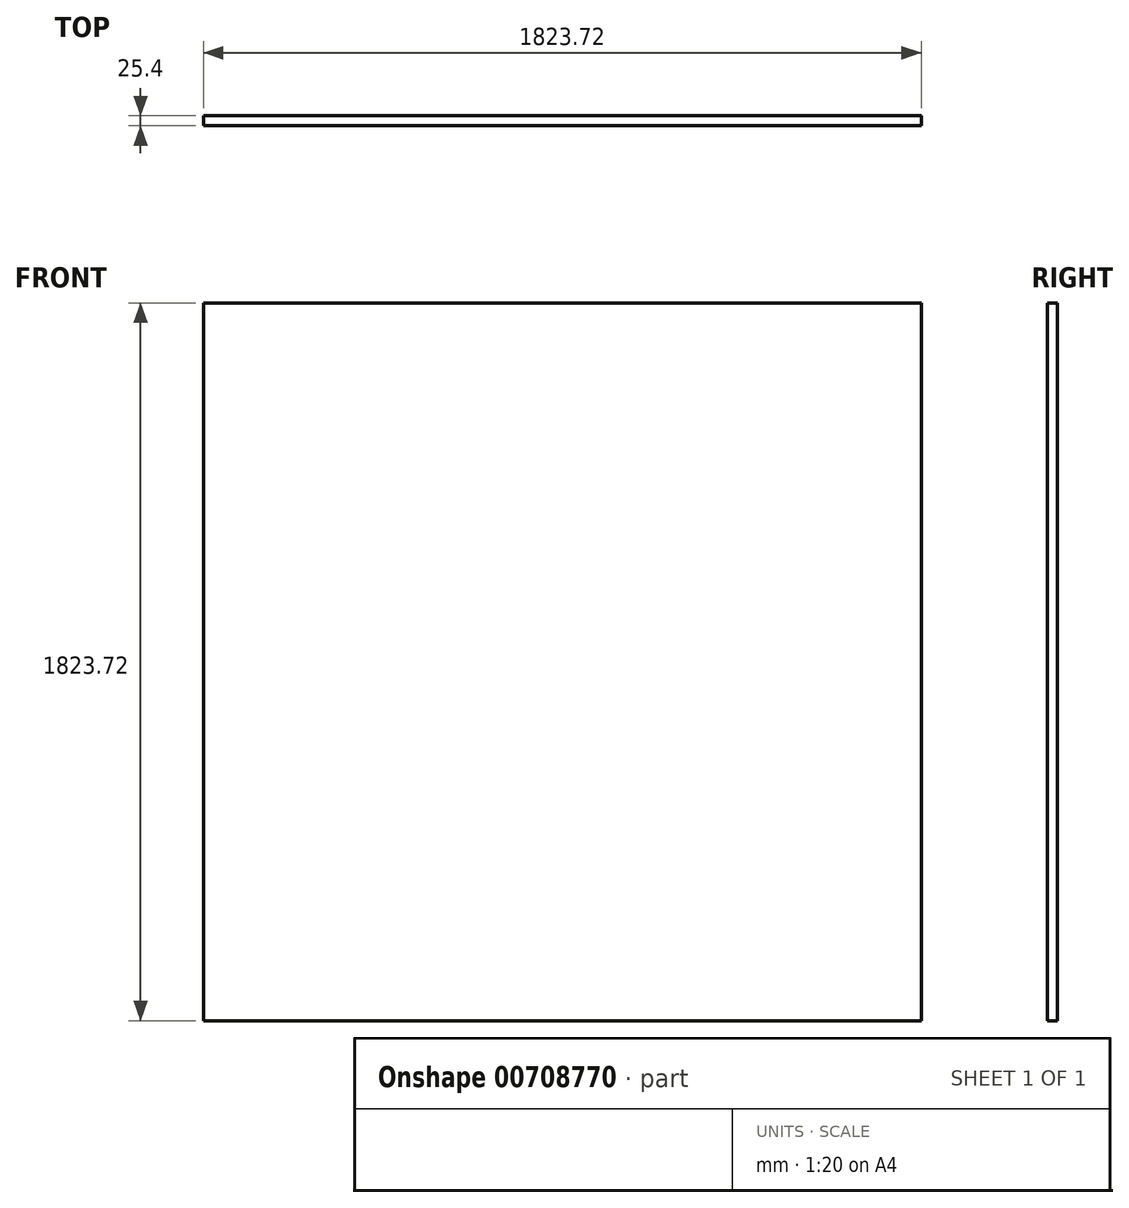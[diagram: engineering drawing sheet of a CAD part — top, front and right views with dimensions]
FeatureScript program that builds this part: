
annotation { "Feature Type Name" : "Feature", "Feature Type Description" : "" }
export const myFeature = defineFeature(function(context is Context, id is Id, definition is map)
    precondition{}
    {
        {
            var Q0;
            Q0=qCreatedBy(makeId("Front.planeOp"),FACE);
            var sketch = newSketch(context, id + "F0", { "sketchPlane" : qUnion([Q0])});
            skLineSegment(sketch, "E0.bottom", {"start": v(0, 0) * mm, "end": v(1823.72, 0) * mm});
            skLineSegment(sketch, "E0.top", {"start": v(0, 1823.72) * mm, "end": v(1823.72, 1823.72) * mm});
            skLineSegment(sketch, "E0.left", {"start": v(0, 0) * mm, "end": v(0, 1823.72) * mm});
            skLineSegment(sketch, "E0.right", {"start": v(1823.72, 0) * mm, "end": v(1823.72, 1823.72) * mm});
            skSolve(sketch);
        }
        {
            var Q0;
            Q0 = qSketchRegion(id + "F0", true);
            extrude(context, id + "F1", {"entities" : qUnion([Q0]), "depth" : 25.4 * mm, "offsetDistance" : 25.4 * mm});
        }
    });
